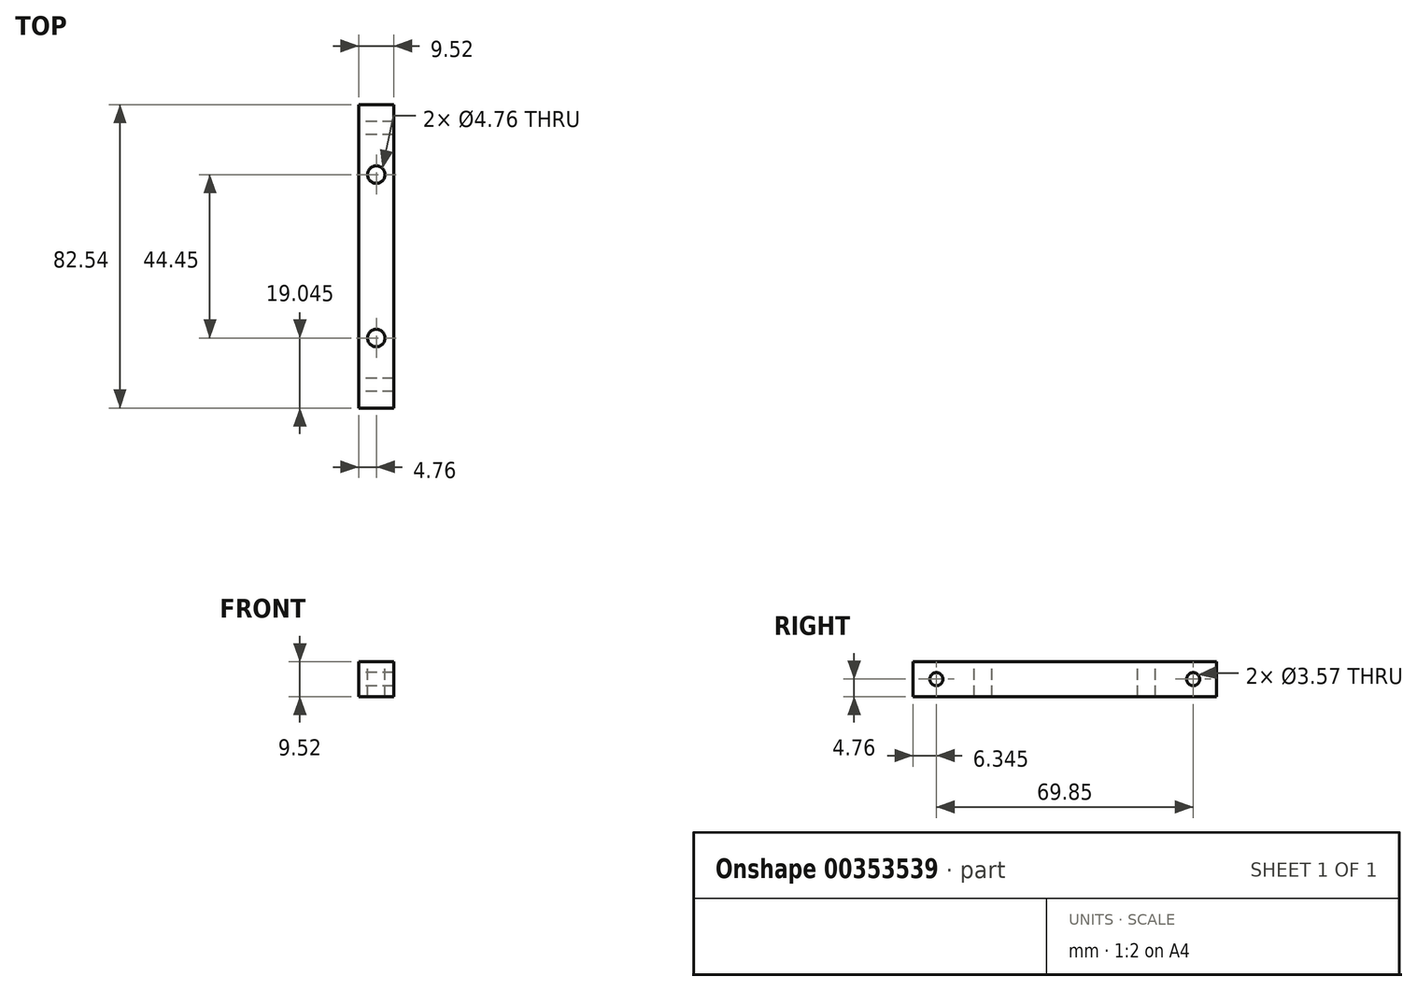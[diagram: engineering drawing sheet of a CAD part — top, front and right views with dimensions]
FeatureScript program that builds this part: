
annotation { "Feature Type Name" : "Feature", "Feature Type Description" : "" }
export const myFeature = defineFeature(function(context is Context, id is Id, definition is map)
    precondition{}
    {
        {
            var Q0;
            Q0=qCreatedBy(makeId("Front.planeOp"),FACE);
            var sketch = newSketch(context, id + "F0", { "sketchPlane" : qUnion([Q0])});
            skLineSegment(sketch, "E0.bottom", {"start": v(4.76, 4.76) * mm, "end": v(-4.76, 4.76) * mm});
            skLineSegment(sketch, "E0.top", {"start": v(4.76, -4.76) * mm, "end": v(-4.76, -4.76) * mm});
            skLineSegment(sketch, "E0.left", {"start": v(4.76, 4.76) * mm, "end": v(4.76, -4.76) * mm});
            skLineSegment(sketch, "E0.right", {"start": v(-4.76, 4.76) * mm, "end": v(-4.76, -4.76) * mm});
            skPoint(sketch, "E0.middle", {"position": v(0, 0) * mm});
            skSolve(sketch);
        }
        {
            var Q0;
            Q0=qSketchRegion(id+"F0",true);
            extrude(context, id + "F1", {"entities" : qUnion([Q0]), "depth" : 82.55 * mm, "symmetric" : true});
        }
        {
            var Q0;
            Q0=makeQuery(id+"F1.opExtrude","SWEPT_FACE",FACE,{"disambiguationData":[OSD([sQuery(id+"F0.wireOp",EDGE,"E0.right")])]});
            var sketch = newSketch(context, id + "F2", { "sketchPlane" : qUnion([Q0])});
            skCircle(sketch, "E1", {"center": v(-34.93, 0) * mm, "radius": 1.79 * mm});
            skCircle(sketch, "E2", {"center": v(34.93, 0) * mm, "radius": 1.79 * mm});
            skSolve(sketch);
        }
        {
            var Q0;
            Q0=makeQuery(id+"F1.opExtrude","SWEPT_FACE",FACE,{"disambiguationData":[OSD([sQuery(id+"F0.wireOp",EDGE,"E0.bottom")])]});
            var sketch = newSketch(context, id + "F3", { "sketchPlane" : qUnion([Q0])});
            skCircle(sketch, "E3", {"center": v(0, 22.23) * mm, "radius": 2.38 * mm});
            skCircle(sketch, "E4", {"center": v(0, -22.23) * mm, "radius": 2.38 * mm});
            skSolve(sketch);
        }
        {
            var Q0;
            Q0=makeQuery(id+"F3.imprint","IMPRINT",FACE,{"disambiguationData":[TD([[makeQuery(id+"F3.imprint","IMPRINT",EDGE,{"derivedFrom":sQuery(id+"F3.wireOp",EDGE,"E3")}),1.0]])]});
            var Q1;
            Q1=makeQuery(id+"F3.imprint","IMPRINT",FACE,{"disambiguationData":[TD([[makeQuery(id+"F3.imprint","IMPRINT",EDGE,{"derivedFrom":sQuery(id+"F3.wireOp",EDGE,"E4")}),1.0]])]});
            extrude(context, id + "F4", {"entities" : qUnion([Q0, Q1]), "operationType" : NewBodyOperationType.REMOVE, "oppositeDirection" : true, "depth" : 9.52 * mm});
        }
        {
            var Q0;
            Q0=makeQuery(id+"F2.imprint","IMPRINT",FACE,{"disambiguationData":[TD([[makeQuery(id+"F2.imprint","IMPRINT",EDGE,{"derivedFrom":sQuery(id+"F2.wireOp",EDGE,"E2")}),1.0]])]});
            var Q1;
            Q1=makeQuery(id+"F2.imprint","IMPRINT",FACE,{"disambiguationData":[TD([[makeQuery(id+"F2.imprint","IMPRINT",EDGE,{"derivedFrom":sQuery(id+"F2.wireOp",EDGE,"E1")}),1.0]])]});
            extrude(context, id + "F5", {"entities" : qUnion([Q0, Q1]), "operationType" : NewBodyOperationType.REMOVE, "oppositeDirection" : true, "depth" : 9.52 * mm});
        }
    });
